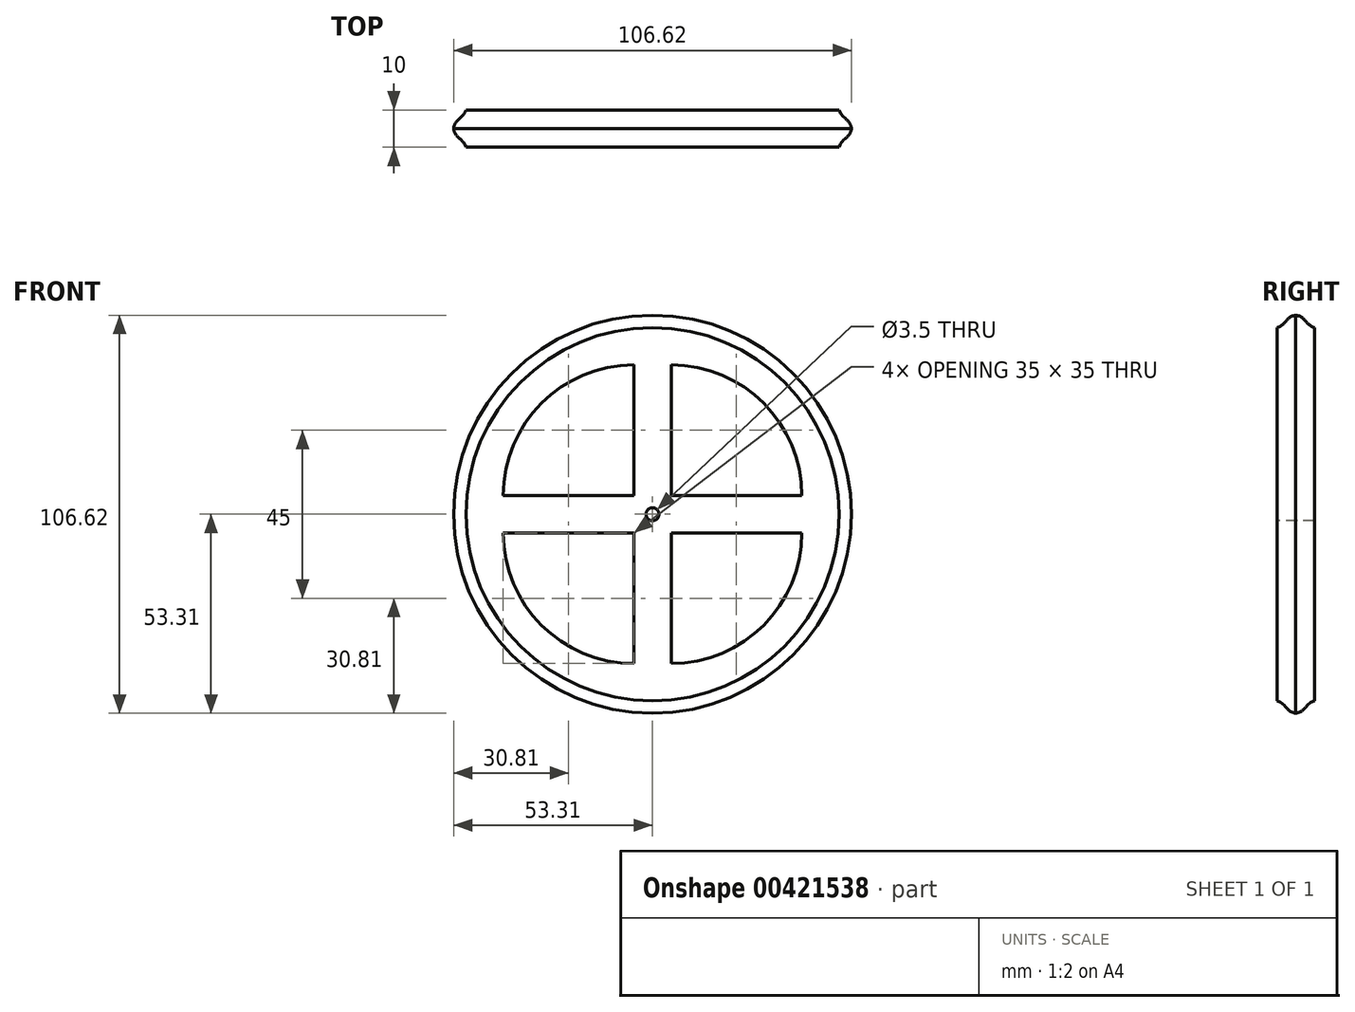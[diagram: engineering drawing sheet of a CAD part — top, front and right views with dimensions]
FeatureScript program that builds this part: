
annotation { "Feature Type Name" : "Feature", "Feature Type Description" : "" }
export const myFeature = defineFeature(function(context is Context, id is Id, definition is map)
    precondition{}
    {
        {
            var Q0;
            Q0=qCreatedBy(makeId("Front.planeOp"),FACE);
            var sketch = newSketch(context, id + "F0", { "sketchPlane" : qUnion([Q0])});
            skCircle(sketch, "E0", {"center": v(0, 0) * mm, "radius": 50 * mm});
            skSolve(sketch);
        }
        {
            var Q0;
            Q0 = qSketchRegion(id + "F0", true);
            extrude(context, id + "F1", {"entities" : qUnion([Q0]), "depth" : 10 * mm});
        }
        {
            var Q0;
            Q0=qCreatedBy(makeId("Right.planeOp"),FACE);
            var sketch = newSketch(context, id + "F2", { "sketchPlane" : qUnion([Q0])});
            skLineSegment(sketch, "E1", {"start": v(0, 0) * mm, "end": v(-41.88, 0) * mm});
            skSolve(sketch);
        }
        {
            var Q0;
            Q0=qCreatedBy(makeId("Right.planeOp"),FACE);
            var sketch = newSketch(context, id + "F3", { "sketchPlane" : qUnion([Q0])});
            skLineSegment(sketch, "E2", {"start": v(0, 50) * mm, "end": v(-10, 50) * mm, "construction": true});
            skPoint(sketch, "E3.1.internal.snap0", {"position": v(-5, 50) * mm});
            skFitSpline(sketch, "E3", {"points": [v(0, 50) * mm, v(-5, 53.3) * mm], "startDerivative": vector(-7.76, 2.57) * mm, "endDerivative": vector(-8.1, 1.22) * mm});
            skLineSegment(sketch, "E4", {"start": v(-5, 53.3) * mm, "end": v(-5, 50) * mm, "construction": true});
            skFitSpline(sketch, "E5.MirrorCS", {"points": [v(-10, 50) * mm, v(-5, 53.3) * mm], "startDerivative": vector(7.76, 2.57) * mm, "endDerivative": vector(8.1, 1.22) * mm});
            skLineSegment(sketch, "E6", {"start": v(0, 50) * mm, "end": v(-10, 50) * mm});
            skSolve(sketch);
        }
        {
            var Q0;
            Q0 = qSketchRegion(id + "F3", true);
            var Q1;
            Q1=sQuery(id+"F2.wireOp",EDGE,"E1");
            revolve(context, id + "F4", {"operationType" : NewBodyOperationType.ADD, "entities" : qUnion([Q0]), "axis" : qUnion([Q1]), "revolveType" : RevolveType.FULL});
        }
        {
            var Q0;
            Q0=makeQuery(id+"F1.opExtrude","CAP_FACE",FACE,{"disambiguationData":[OSD([sQuery(id+"F0.wireOp",EDGE,"E0")])],"isStart":false});
            var sketch = newSketch(context, id + "F5", { "sketchPlane" : qUnion([Q0])});
            skCircle(sketch, "E7", {"center": v(0, 0) * mm, "radius": 1.75 * mm});
            skSolve(sketch);
        }
        {
            var Q0;
            Q0 = qSketchRegion(id + "F5", true);
            extrude(context, id + "F6", {"entities" : qUnion([Q0]), "operationType" : NewBodyOperationType.REMOVE, "endBound" : BoundingType.THROUGH_ALL, "oppositeDirection" : true, "depth" : 25 * mm});
        }
        {
            var Q0;
            Q0=makeQuery(id+"F1.opExtrude","CAP_FACE",FACE,{"disambiguationData":[OSD([sQuery(id+"F0.wireOp",EDGE,"E0")])],"isStart":false});
            var sketch = newSketch(context, id + "F7", { "sketchPlane" : qUnion([Q0])});
            skLineSegment(sketch, "E8", {"start": v(-5, 5) * mm, "end": v(-40, 5) * mm});
            skLineSegment(sketch, "E9", {"start": v(-5, 5) * mm, "end": v(-5, 40) * mm});
            skArc(sketch, "E10", {"start": v(-5, 40) * mm, "mid": v(-29.75, 29.75) * mm, "end": v(-40, 5) * mm});
            skArc(sketch, "E11.MirrorCS", {"start": v(5, 40) * mm, "mid": v(29.75, 29.75) * mm, "end": v(40, 5) * mm});
            skLineSegment(sketch, "E12.MirrorCS", {"start": v(5, 5) * mm, "end": v(5, 40) * mm});
            skLineSegment(sketch, "E13.MirrorCS", {"start": v(5, 5) * mm, "end": v(40, 5) * mm});
            skLineSegment(sketch, "E14.MirrorCS", {"start": v(5, -5) * mm, "end": v(40, -5) * mm});
            skArc(sketch, "E15.MirrorCS", {"start": v(5, -40) * mm, "mid": v(29.75, -29.75) * mm, "end": v(40, -5) * mm});
            skLineSegment(sketch, "E16.MirrorCS", {"start": v(5, -5) * mm, "end": v(5, -40) * mm});
            skLineSegment(sketch, "E17.MirrorCS", {"start": v(-5, -5) * mm, "end": v(-5, -40) * mm});
            skLineSegment(sketch, "E18.MirrorCS", {"start": v(-5, -5) * mm, "end": v(-40, -5) * mm});
            skArc(sketch, "E19.MirrorCS", {"start": v(-5, -40) * mm, "mid": v(-29.75, -29.75) * mm, "end": v(-40, -5) * mm});
            skSolve(sketch);
        }
        {
            var Q0;
            Q0 = qSketchRegion(id + "F7", true);
            extrude(context, id + "F8", {"entities" : qUnion([Q0]), "operationType" : NewBodyOperationType.REMOVE, "endBound" : BoundingType.THROUGH_ALL, "oppositeDirection" : true, "depth" : 25 * mm});
        }
    });
